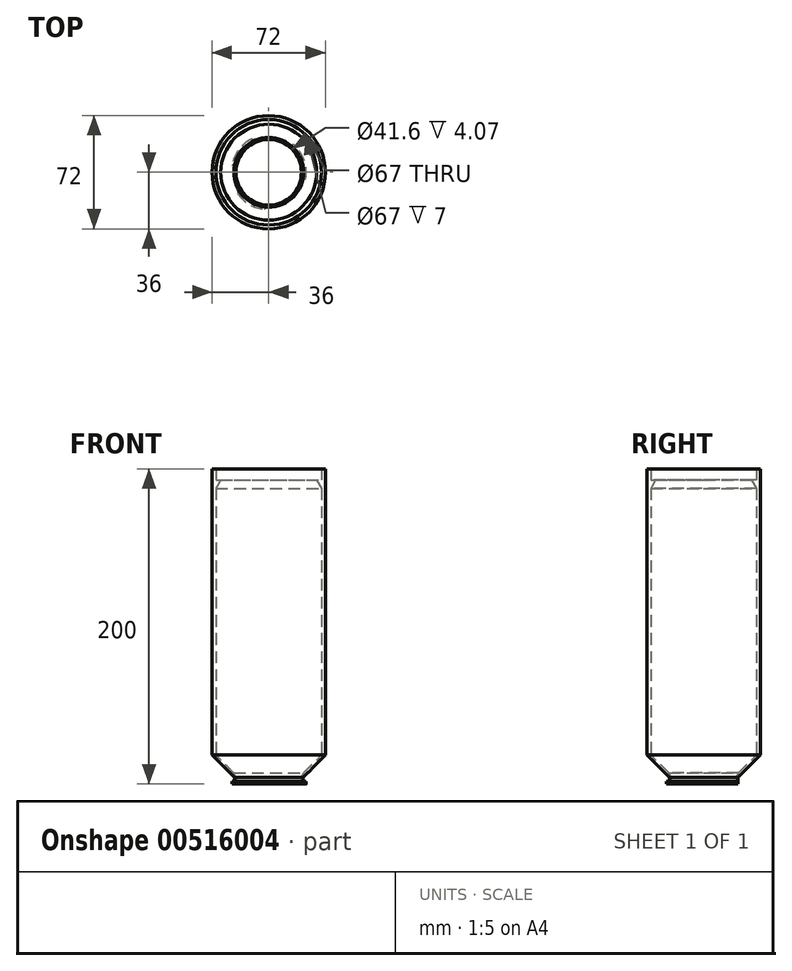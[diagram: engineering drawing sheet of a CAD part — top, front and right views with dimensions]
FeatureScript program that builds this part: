
annotation { "Feature Type Name" : "Feature", "Feature Type Description" : "" }
export const myFeature = defineFeature(function(context is Context, id is Id, definition is map)
    precondition{}
    {
        {
            var Q0;
            Q0=qCreatedBy(makeId("Top.planeOp"),FACE);
            var sketch = newSketch(context, id + "F0", { "sketchPlane" : qUnion([Q0])});
            skCircle(sketch, "E0", {"center": v(0, 0) * mm, "radius": 20.8 * mm});
            skArc(sketch, "E1", {"start": v(-21.6, 3.3) * mm, "mid": v(-21.3, -4.85) * mm, "end": v(-18.04, -12.33) * mm});
            skArc(sketch, "E2", {"start": v(-10.87, 21.18) * mm, "mid": v(-19, 14.33) * mm, "end": v(-23.35, 4.62) * mm});
            skPoint(sketch, "E3", {"position": v(-9.12, 19.86) * mm});
            skPoint(sketch, "E4", {"position": v(14.37, 16.46) * mm});
            skPoint(sketch, "E5", {"position": v(21.5, -3.88) * mm});
            skPoint(sketch, "E6", {"position": v(-2.78, -21.67) * mm});
            skPoint(sketch, "E7", {"position": v(-18.04, -12.33) * mm});
            skPoint(sketch, "E8", {"position": v(-21.6, 3.3) * mm});
            skLineSegment(sketch, "E9", {"start": v(-9.12, 19.86) * mm, "end": v(-21.6, 3.3) * mm, "construction": true});
            skLineSegment(sketch, "E10", {"start": v(-21.6, 3.3) * mm, "end": v(-22.88, -5.04) * mm, "construction": true});
            skLineSegment(sketch, "E11", {"start": v(-21.6, 3.3) * mm, "end": v(-23.35, 4.62) * mm});
            skLineSegment(sketch, "E12", {"start": v(-9.12, 19.86) * mm, "end": v(-0.54, 23.8) * mm, "construction": true});
            skLineSegment(sketch, "E13", {"start": v(14.37, 16.46) * mm, "end": v(21.5, -3.88) * mm, "construction": true});
            skLineSegment(sketch, "E14", {"start": v(14.37, 16.46) * mm, "end": v(8.84, 21.29) * mm, "construction": true});
            skLineSegment(sketch, "E15", {"start": v(14.37, 16.46) * mm, "end": v(15.65, 17.93) * mm});
            skLineSegment(sketch, "E16", {"start": v(21.5, -3.88) * mm, "end": v(20, -12.24) * mm, "construction": true});
            skLineSegment(sketch, "E17", {"start": v(21.5, -3.88) * mm, "end": v(23.42, -4.23) * mm});
            skLineSegment(sketch, "E18", {"start": v(-2.78, -21.67) * mm, "end": v(4.8, -22.65) * mm, "construction": true});
            skLineSegment(sketch, "E19", {"start": v(-2.78, -21.67) * mm, "end": v(-2.78, -23.64) * mm});
            skLineSegment(sketch, "E20", {"start": v(-18.04, -12.33) * mm, "end": v(-21.8, -6.84) * mm, "construction": true});
            skLineSegment(sketch, "E21", {"start": v(-18.04, -12.33) * mm, "end": v(-19.65, -13.43) * mm});
            skLineSegment(sketch, "E22", {"start": v(-9.12, 19.86) * mm, "end": v(-10.87, 21.18) * mm});
            skArc(sketch, "E23.trimOffspring", {"start": v(23.42, -4.23) * mm, "mid": v(22.46, 7.87) * mm, "end": v(15.65, 17.93) * mm});
            skArc(sketch, "E24.trimOffspring", {"start": v(-19.65, -13.43) * mm, "mid": v(-12.32, -20.36) * mm, "end": v(-2.78, -23.64) * mm});
            skArc(sketch, "E25.trimOffspring", {"start": v(-2.78, -21.67) * mm, "mid": v(12.91, -17.63) * mm, "end": v(21.5, -3.88) * mm});
            skArc(sketch, "E26.trimOffspring", {"start": v(14.37, 16.46) * mm, "mid": v(3.13, 21.63) * mm, "end": v(-9.12, 19.86) * mm});
            skSolve(sketch);
        }
        {
            var Q0;
            Q0=makeQuery(id+"F0.imprint","IMPRINT",FACE,{"disambiguationData":[TD([[makeQuery(id+"F0.imprint","IMPRINT",EDGE,{"derivedFrom":sQuery(id+"F0.wireOp",EDGE,"E0")}),-1.0]])]});
            extrude(context, id + "F1", {"entities" : qUnion([Q0]), "depth" : 1.65 * mm, "offsetDistance" : 25.4 * mm});
        }
        {
            var Q0;
            Q0=makeQuery(id+"F1.opExtrude","CAP_FACE",FACE,{"disambiguationData":[OSD([sQuery(id+"F0.wireOp",EDGE,"E0"),sQuery(id+"F0.wireOp",EDGE,"E1"),sQuery(id+"F0.wireOp",EDGE,"E2"),sQuery(id+"F0.wireOp",EDGE,"E11"),sQuery(id+"F0.wireOp",EDGE,"E15"),sQuery(id+"F0.wireOp",EDGE,"E17"),sQuery(id+"F0.wireOp",EDGE,"E19"),sQuery(id+"F0.wireOp",EDGE,"E21"),sQuery(id+"F0.wireOp",EDGE,"E22"),sQuery(id+"F0.wireOp",EDGE,"E23.trimOffspring"),sQuery(id+"F0.wireOp",EDGE,"E24.trimOffspring"),sQuery(id+"F0.wireOp",EDGE,"E25.trimOffspring"),sQuery(id+"F0.wireOp",EDGE,"E26.trimOffspring")])],"isStart":false});
            var sketch = newSketch(context, id + "F2", { "sketchPlane" : qUnion([Q0])});
            skCircle(sketch, "E27", {"center": v(0, 0) * mm, "radius": 21.79 * mm});
            skCircle(sketch, "E28.0", {"center": v(0, 0) * mm, "radius": 20.8 * mm});
            skSolve(sketch);
        }
        {
            var Q0;
            Q0=makeQuery(id+"F2.imprint","IMPRINT",FACE,{"disambiguationData":[TD([[makeQuery(id+"F2.imprint","IMPRINT",EDGE,{"derivedFrom":sQuery(id+"F2.wireOp",EDGE,"E27")}),1.0]])]});
            extrude(context, id + "F3", {"entities" : qUnion([Q0]), "operationType" : NewBodyOperationType.ADD, "depth" : 4.07 * mm - 1.65 * mm, "offsetDistance" : 25.4 * mm});
        }
        {
            var Q0;
            Q0=qCreatedBy(makeId("Right.planeOp"),FACE);
            var sketch = newSketch(context, id + "F4", { "sketchPlane" : qUnion([Q0])});
            skLineSegment(sketch, "E29", {"start": v(0, 0) * mm, "end": v(0, 200) * mm, "construction": true});
            skLineSegment(sketch, "E30", {"start": v(-36, 200) * mm, "end": v(36, 200) * mm, "construction": true});
            skLineSegment(sketch, "E31.0", {"start": v(-20.8, 4.07) * mm, "end": v(20.8, 4.07) * mm, "construction": true});
            skLineSegment(sketch, "E32", {"start": v(-33.5, 200) * mm, "end": v(-36, 200) * mm});
            skLineSegment(sketch, "E33", {"start": v(-21.79, 4.07) * mm, "end": v(-20.8, 4.07) * mm});
            skLineSegment(sketch, "E34", {"start": v(-36, 200) * mm, "end": v(-36, 18.28) * mm});
            skLineSegment(sketch, "E35", {"start": v(-36, 18.28) * mm, "end": v(-21.8, 4.07) * mm});
            skLineSegment(sketch, "E36", {"start": v(-33.5, 200) * mm, "end": v(-33.5, 193) * mm});
            skLineSegment(sketch, "E37", {"start": v(-33.5, 18.28) * mm, "end": v(-22.15, 6.93) * mm});
            skLineSegment(sketch, "E38", {"start": v(-22.15, 6.93) * mm, "end": v(-20.8, 4.07) * mm});
            skLineSegment(sketch, "E39", {"start": v(-33.5, 193) * mm, "end": v(-30.5, 193) * mm});
            skLineSegment(sketch, "E40", {"start": v(-30.5, 193) * mm, "end": v(-33.5, 187.8) * mm});
            skLineSegment(sketch, "E41", {"start": v(-33.5, 187.8) * mm, "end": v(-19.98, 187.8) * mm, "construction": true});
            skLineSegment(sketch, "E42.trimOffspring", {"start": v(-33.5, 187.8) * mm, "end": v(-33.5, 18.28) * mm});
            skSolve(sketch);
        }
        {
            var Q0;
            Q0=makeQuery(id+"F4.imprint","IMPRINT",FACE,{"disambiguationData":[TD([[makeQuery(id+"F4.imprint","IMPRINT",EDGE,{"derivedFrom":sQuery(id+"F4.wireOp",EDGE,"E32")}),1.0]])]});
            var Q1;
            Q1=sQuery(id+"F4.wireOp",EDGE,"E29");
            revolve(context, id + "F5", {"operationType" : NewBodyOperationType.ADD, "entities" : qUnion([Q0]), "axis" : qUnion([Q1]), "revolveType" : RevolveType.FULL});
        }
    });
